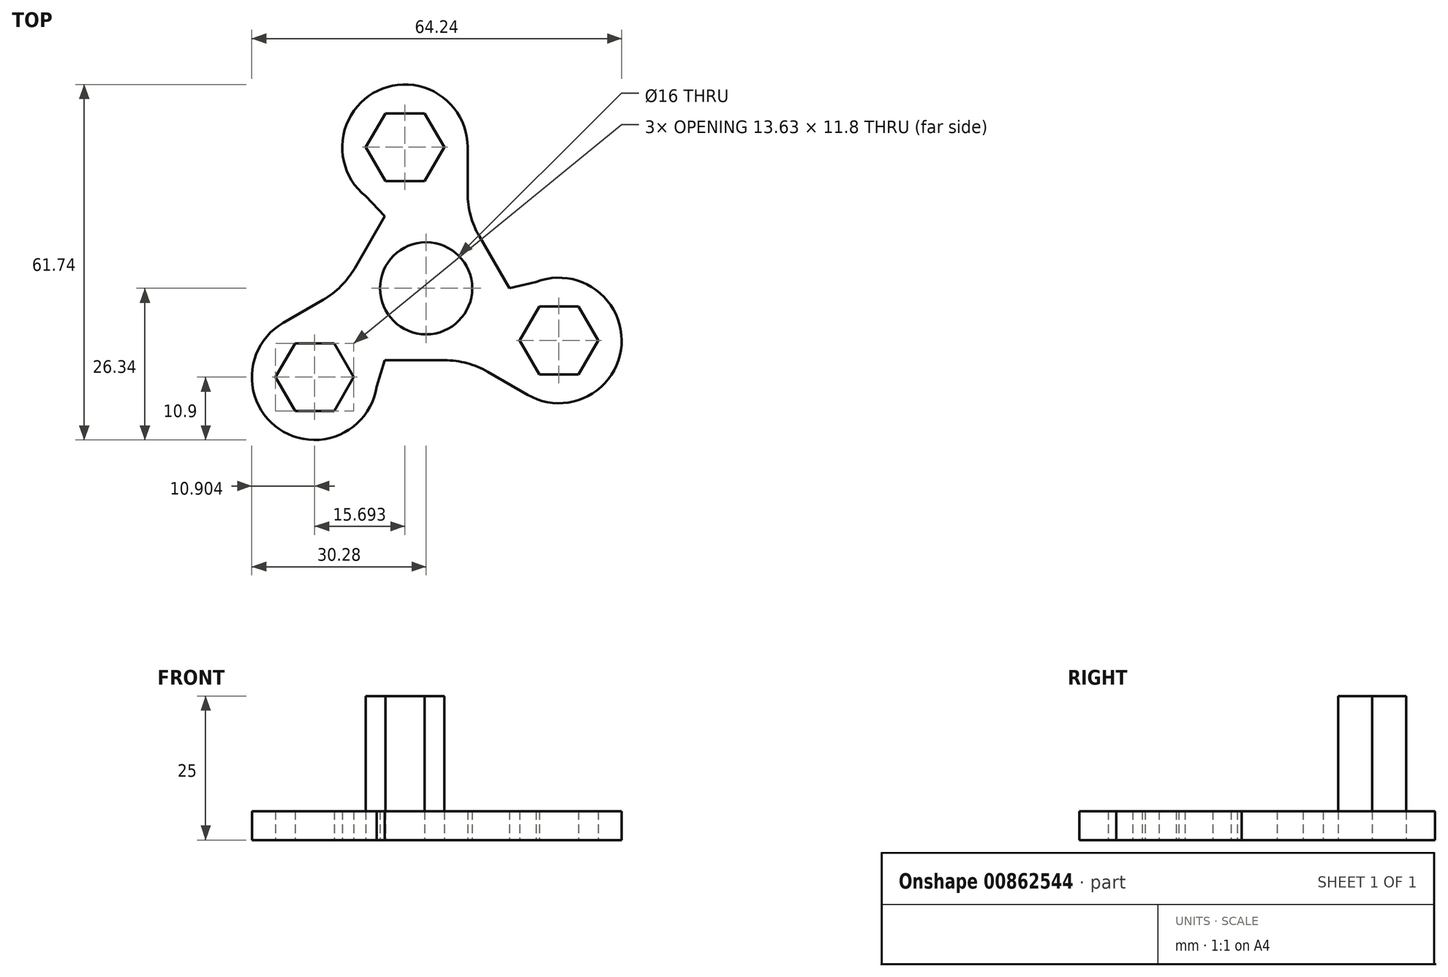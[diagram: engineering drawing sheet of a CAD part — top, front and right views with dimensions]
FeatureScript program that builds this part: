
annotation { "Feature Type Name" : "Feature", "Feature Type Description" : "" }
export const myFeature = defineFeature(function(context is Context, id is Id, definition is map)
    precondition{}
    {
        {
            var Q0;
            Q0=qCreatedBy(makeId("Top.planeOp"),FACE);
            var sketch = newSketch(context, id + "F0", { "sketchPlane" : qUnion([Q0])});
            skCircle(sketch, "E0", {"center": v(0, 0) * mm, "radius": 8 * mm});
            skCircle(sketch, "E1.cCircle", {"center": v(0, 0) * mm, "radius": 12.5 * mm, "construction": true});
            skLineSegment(sketch, "E1.0", {"start": v(-7.22, 12.5) * mm, "end": v(7.22, 12.5) * mm});
            skLineSegment(sketch, "E1.1", {"start": v(7.22, 12.5) * mm, "end": v(14.43, 0) * mm});
            skLineSegment(sketch, "E1.2", {"start": v(14.43, 0) * mm, "end": v(7.22, -12.5) * mm});
            skLineSegment(sketch, "E1.3", {"start": v(7.22, -12.5) * mm, "end": v(-7.22, -12.5) * mm});
            skLineSegment(sketch, "E1.4", {"start": v(-7.22, -12.5) * mm, "end": v(-14.43, 0) * mm});
            skLineSegment(sketch, "E1.5", {"start": v(-14.43, 0) * mm, "end": v(-7.22, 12.5) * mm});
            skPoint(sketch, "E1.0.midPoint", {"position": v(0, 12.5) * mm});
            skCircle(sketch, "E2.cCircle", {"center": v(-3.68, 24.5) * mm, "radius": 5.9 * mm, "construction": true});
            skLineSegment(sketch, "E2.0", {"start": v(-7.09, 30.4) * mm, "end": v(-0.28, 30.4) * mm});
            skLineSegment(sketch, "E2.1", {"start": v(-0.28, 30.4) * mm, "end": v(3.13, 24.5) * mm});
            skLineSegment(sketch, "E2.2", {"start": v(3.13, 24.5) * mm, "end": v(-0.28, 18.6) * mm});
            skLineSegment(sketch, "E2.3", {"start": v(-0.28, 18.6) * mm, "end": v(-7.09, 18.6) * mm});
            skLineSegment(sketch, "E2.4", {"start": v(-7.09, 18.6) * mm, "end": v(-10.5, 24.5) * mm});
            skLineSegment(sketch, "E2.5", {"start": v(-10.5, 24.5) * mm, "end": v(-7.09, 30.4) * mm});
            skPoint(sketch, "E2.0.midPoint", {"position": v(-3.68, 30.4) * mm});
            skLineSegment(sketch, "E3", {"start": v(7.22, 12.5) * mm, "end": v(7.22, 24.5) * mm});
            skArc(sketch, "E4", {"start": v(7.22, 24.5) * mm, "mid": v(-8.4, 34.33) * mm, "end": v(-10.5, 16) * mm});
            skLineSegment(sketch, "E5", {"start": v(-10.5, 16) * mm, "end": v(-7.22, 12.5) * mm});
            skSolve(sketch);
        }
        {
            var Q0;
            Q0=makeQuery(id+"F0.imprint","IMPRINT",FACE,{"disambiguationData":[TD([[makeQuery(id+"F0.imprint","IMPRINT",EDGE,{"derivedFrom":sQuery(id+"F0.wireOp",EDGE,"E0")}),-1.0]])]});
            extrude(context, id + "F1", {"entities" : qUnion([Q0]), "depth" : 5 * mm, "offsetDistance" : 25 * mm});
        }
        {
            var Q0;
            Q0=makeQuery(id+"F0.imprint","IMPRINT",FACE,{"disambiguationData":[TD([[makeQuery(id+"F0.imprint","IMPRINT",EDGE,{"derivedFrom":sQuery(id+"F0.wireOp",EDGE,"E1.0")}),1.0]])]});
            var Q1;
            Q1=makeQuery(id+"F0.imprint","IMPRINT",FACE,{"disambiguationData":[TD([[makeQuery(id+"F0.imprint","IMPRINT",EDGE,{"derivedFrom":sQuery(id+"F0.wireOp",EDGE,"E2.0")}),1.0]])]});
            var Q2;
            {var subQ0=sQuery(id+"F0.wireOp",EDGE,"f425258b-878d-4473-b1fe-abe1052e9d06.2");var subQ1=sQuery(id+"F0.wireOp",EDGE,"f425258b-878d-4473-b1fe-abe1052e9d06.cCircle");var subQ2=makeQuery(id+"F0.imprint","INTERSECT",VERTEX,{"derivedFrom":[subQ1,subQ0]});Q2=makeQuery(id+"F0.imprint","IMPRINT",FACE,{"disambiguationData":[TD([[makeQuery(id+"F0.imprint","IMPRINT",EDGE,{"disambiguationData":[TD([[subQ2,1.0]])],"derivedFrom":subQ1}),-1.0]])]});}
            var Q3;
            {var subQ0=sQuery(id+"F0.wireOp",EDGE,"f425258b-878d-4473-b1fe-abe1052e9d06.4");var subQ1=sQuery(id+"F0.wireOp",EDGE,"f425258b-878d-4473-b1fe-abe1052e9d06.cCircle");var subQ2=makeQuery(id+"F0.imprint","INTERSECT",VERTEX,{"derivedFrom":[subQ1,subQ0]});Q3=makeQuery(id+"F0.imprint","IMPRINT",FACE,{"disambiguationData":[TD([[makeQuery(id+"F0.imprint","IMPRINT",EDGE,{"disambiguationData":[TD([[subQ2,-1.0]])],"derivedFrom":subQ1}),-1.0]])]});}
            extrude(context, id + "F2", {"entities" : qUnion([Q0, Q1, Q2, Q3]), "depth" : 5 * mm, "offsetDistance" : 25 * mm});
        }
        {
            var Q0;
            Q0=makeQuery(id+"F2.opExtrude","SWEPT_BODY",BODY,{"disambiguationData":[OSD([sQuery(id+"F0.wireOp",EDGE,"f425258b-878d-4473-b1fe-abe1052e9d06.0"),sQuery(id+"F0.wireOp",EDGE,"f425258b-878d-4473-b1fe-abe1052e9d06.1"),sQuery(id+"F0.wireOp",EDGE,"f425258b-878d-4473-b1fe-abe1052e9d06.2"),sQuery(id+"F0.wireOp",EDGE,"f425258b-878d-4473-b1fe-abe1052e9d06.3"),sQuery(id+"F0.wireOp",EDGE,"f425258b-878d-4473-b1fe-abe1052e9d06.4"),sQuery(id+"F0.wireOp",EDGE,"f425258b-878d-4473-b1fe-abe1052e9d06.5"),sQuery(id+"F0.wireOp",EDGE,"E2.0"),sQuery(id+"F0.wireOp",EDGE,"E2.1"),sQuery(id+"F0.wireOp",EDGE,"E2.2"),sQuery(id+"F0.wireOp",EDGE,"E2.3"),sQuery(id+"F0.wireOp",EDGE,"E2.4"),sQuery(id+"F0.wireOp",EDGE,"E2.5")])]});
            var Q1;
            Q1=sQuery(id+"F0.wireOp",EDGE,"E1.cCircle");
            circularPattern(context, id + "F3", {"operationType" : NewBodyOperationType.ADD, "entities" : qUnion([Q0]), "axis" : qUnion([Q1]), "angle" : 360 * degree, "instanceCount" : 3, "equalSpace" : true});
        }
        {
            var Q0;
            Q0=makeQuery(id+"F0.imprint","IMPRINT",FACE,{"disambiguationData":[TD([[makeQuery(id+"F0.imprint","IMPRINT",EDGE,{"derivedFrom":sQuery(id+"F0.wireOp",EDGE,"E2.0")}),-1.0]])]});
            extrude(context, id + "F4", {"entities" : qUnion([Q0]), "depth" : 25 * mm, "offsetDistance" : 25 * mm});
        }
        {
            var Q0;
            {var subQ0=sQuery(id+"F0.wireOp",EDGE,"E3");var subQ1=sQuery(id+"F0.wireOp",EDGE,"E1.1");var subQ2=sQuery(id+"F0.wireOp",EDGE,"E1.0");Q0=makeQuery(id+"F3.boolean.opBoolean","MERGE",EDGE,{"derivedFrom":[makeQuery(id+"F1.opExtrude","SWEPT_EDGE",EDGE,{"disambiguationData":[OSD([subQ2,subQ1,subQ0])]}),makeQuery(id+"F2.opExtrude","SWEPT_EDGE",EDGE,{"disambiguationData":[OSD([subQ2,subQ1,subQ0])]})]});}
            var Q1;
            Q1=makeQuery(id+"F3.boolean.opBoolean","MERGE",EDGE,{"derivedFrom":[makeQuery(id+"F1.opExtrude","SWEPT_EDGE",EDGE,{"disambiguationData":[OSD([sQuery(id+"F0.wireOp",EDGE,"E1.2"),sQuery(id+"F0.wireOp",EDGE,"E1.3")])]}),makeQuery(id+"F3.opPattern","COPY",EDGE,{"derivedFrom":makeQuery(id+"F2.opExtrude","SWEPT_EDGE",EDGE,{"disambiguationData":[OSD([sQuery(id+"F0.wireOp",EDGE,"E1.0"),sQuery(id+"F0.wireOp",EDGE,"E1.1"),sQuery(id+"F0.wireOp",EDGE,"E3")])]}),"instanceName":"2"})]});
            var Q2;
            Q2=makeQuery(id+"F3.boolean.opBoolean","MERGE",EDGE,{"derivedFrom":[makeQuery(id+"F1.opExtrude","SWEPT_EDGE",EDGE,{"disambiguationData":[OSD([sQuery(id+"F0.wireOp",EDGE,"E1.4"),sQuery(id+"F0.wireOp",EDGE,"E1.5")])]}),makeQuery(id+"F3.opPattern","COPY",EDGE,{"derivedFrom":makeQuery(id+"F2.opExtrude","SWEPT_EDGE",EDGE,{"disambiguationData":[OSD([sQuery(id+"F0.wireOp",EDGE,"E1.0"),sQuery(id+"F0.wireOp",EDGE,"E1.1"),sQuery(id+"F0.wireOp",EDGE,"E3")])]}),"instanceName":"1"})]});
            fillet(context, id + "F5", {"entities" : qUnion([Q0, Q1, Q2]), "radius" : 15 * mm, "tangentPropagation" : true, "allowEdgeOverflow" : false});
        }
    });
